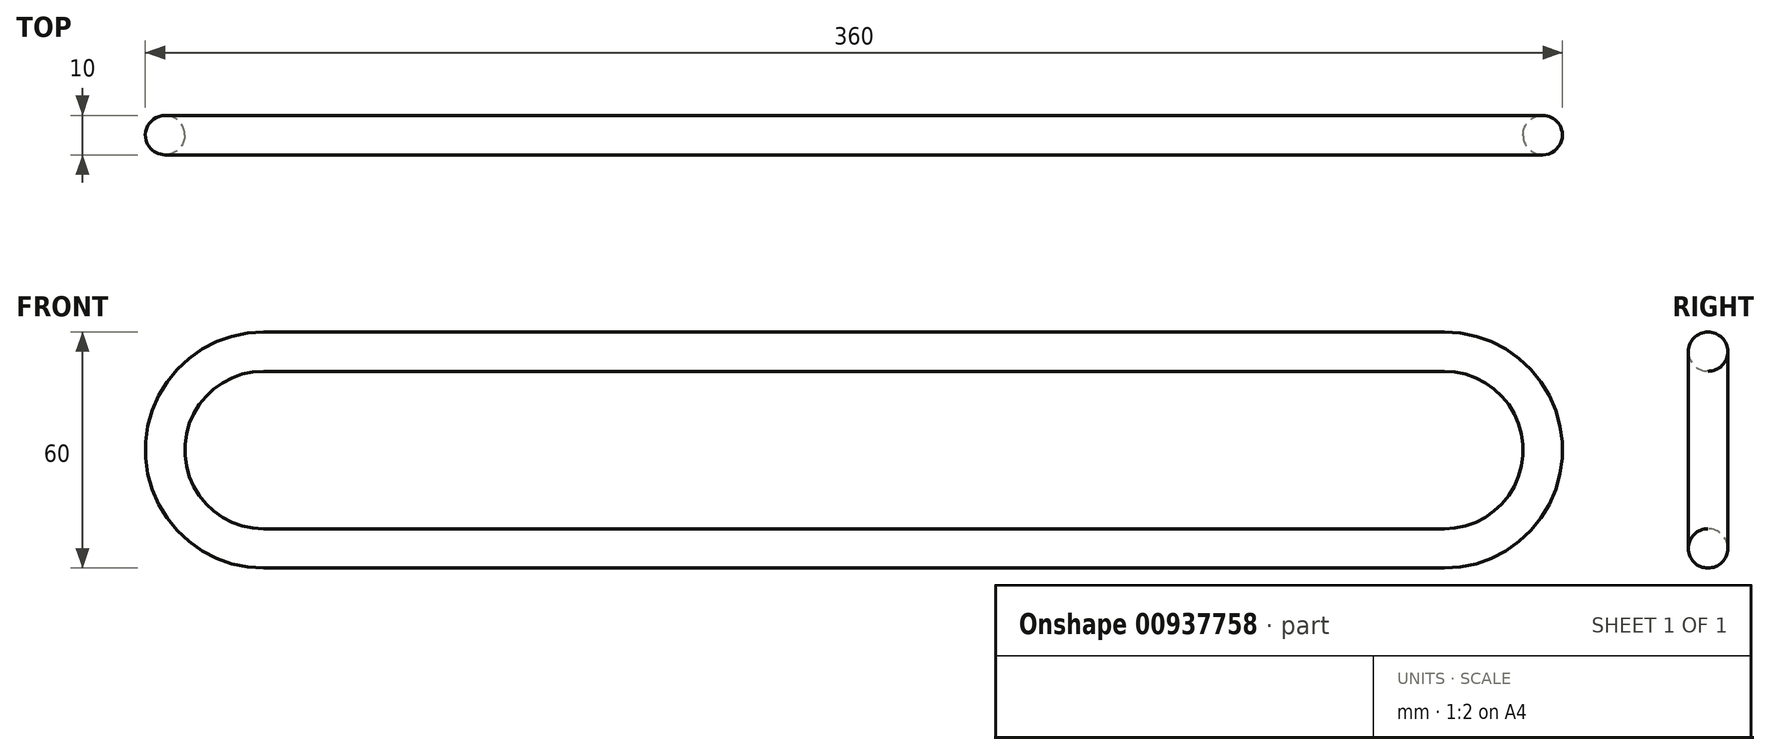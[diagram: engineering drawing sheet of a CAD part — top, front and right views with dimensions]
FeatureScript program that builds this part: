
annotation { "Feature Type Name" : "Feature", "Feature Type Description" : "" }
export const myFeature = defineFeature(function(context is Context, id is Id, definition is map)
    precondition{}
    {
        {
            var Q0;
            Q0=qCreatedBy(makeId("Front.planeOp"),FACE);
            var sketch = newSketch(context, id + "F0", { "sketchPlane" : qUnion([Q0])});
            skArc(sketch, "E0", {"start": v(-150, 25) * mm, "mid": v(-175, 0) * mm, "end": v(-150, -25) * mm});
            skArc(sketch, "E1", {"start": v(150, -25) * mm, "mid": v(175, 0) * mm, "end": v(150, 25) * mm});
            skLineSegment(sketch, "E2", {"start": v(-150, 25) * mm, "end": v(150, 25) * mm});
            skLineSegment(sketch, "E3", {"start": v(150, -25) * mm, "end": v(-150, -25) * mm});
            skSolve(sketch);
        }
        {
            var Q0;
            Q0=qCreatedBy(makeId("Right.planeOp"),FACE);
            var sketch = newSketch(context, id + "F1", { "sketchPlane" : qUnion([Q0])});
            skPoint(sketch, "E4", {"position": v(0, 25) * mm});
            skCircle(sketch, "E5", {"center": v(0, 25) * mm, "radius": 5 * mm});
            skSolve(sketch);
        }
        {
            var Q0;
            Q0=makeQuery(id+"F1.imprint","IMPRINT",FACE,{"disambiguationData":[TD([[makeQuery(id+"F1.imprint","IMPRINT",EDGE,{"derivedFrom":sQuery(id+"F1.wireOp",EDGE,"E5")}),1.0]])]});
            var Q1;
            Q1=sQuery(id+"F0.wireOp",EDGE,"E2");
            var Q2;
            Q2=sQuery(id+"F0.wireOp",EDGE,"E0");
            var Q3;
            Q3=sQuery(id+"F0.wireOp",EDGE,"E3");
            var Q4;
            Q4=sQuery(id+"F0.wireOp",EDGE,"E1");
            sweep(context, id + "F2", {"profiles" : qUnion([Q0]), "path" : qUnion([Q1, Q2, Q3, Q4])});
        }
    });
